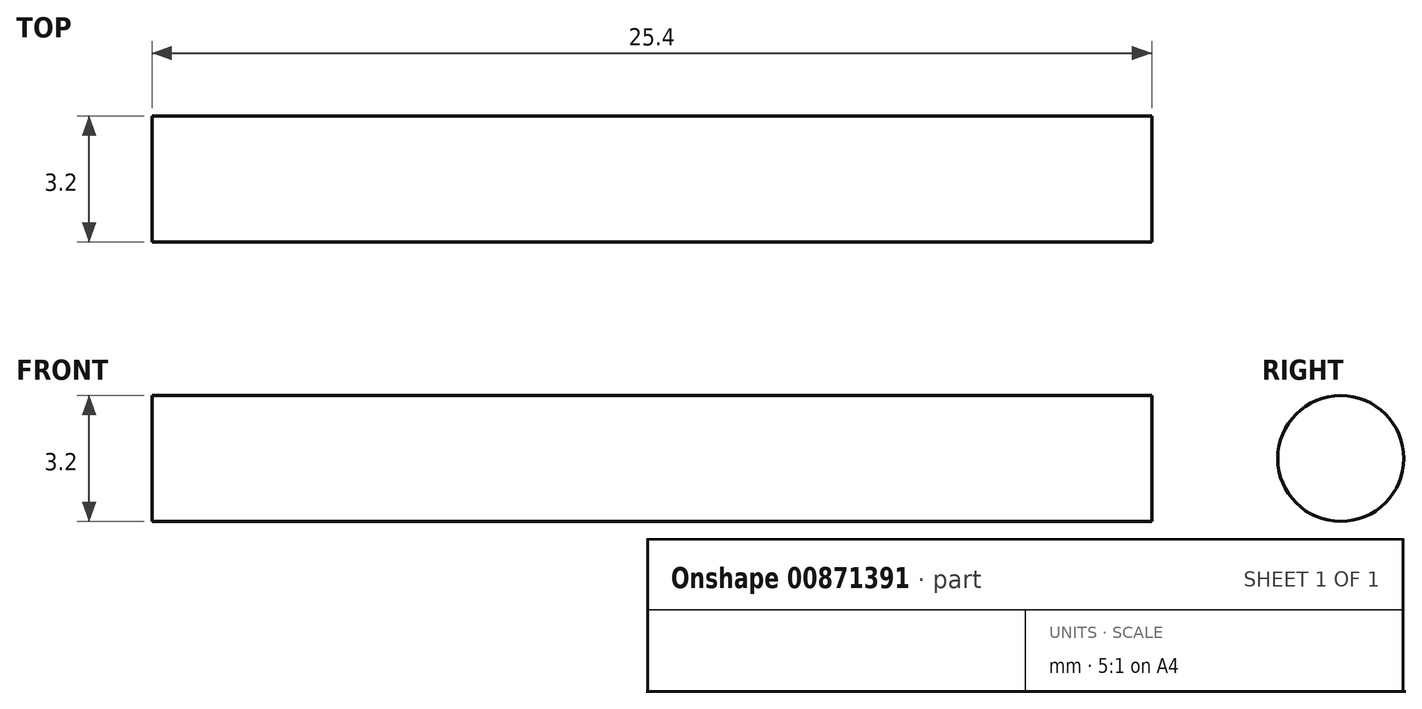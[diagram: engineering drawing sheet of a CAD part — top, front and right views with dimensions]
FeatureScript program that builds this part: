
annotation { "Feature Type Name" : "Feature", "Feature Type Description" : "" }
export const myFeature = defineFeature(function(context is Context, id is Id, definition is map)
    precondition{}
    {
        {
            var Q0;
            Q0=qCreatedBy(makeId("Right.planeOp"),FACE);
            var sketch = newSketch(context, id + "F0", { "sketchPlane" : qUnion([Q0])});
            skCircle(sketch, "E0", {"center": v(0, 0) * mm, "radius": 1.6 * mm});
            skSolve(sketch);
        }
        {
            var Q0;
            Q0=makeQuery(id+"F0.imprint","IMPRINT",FACE,{"disambiguationData":[TD([[makeQuery(id+"F0.imprint","IMPRINT",EDGE,{"derivedFrom":sQuery(id+"F0.wireOp",EDGE,"E0")}),1.0]])]});
            extrude(context, id + "F1", {"entities" : qUnion([Q0]), "depth" : 25.4 * mm, "offsetDistance" : 25.4 * mm});
        }
    });
